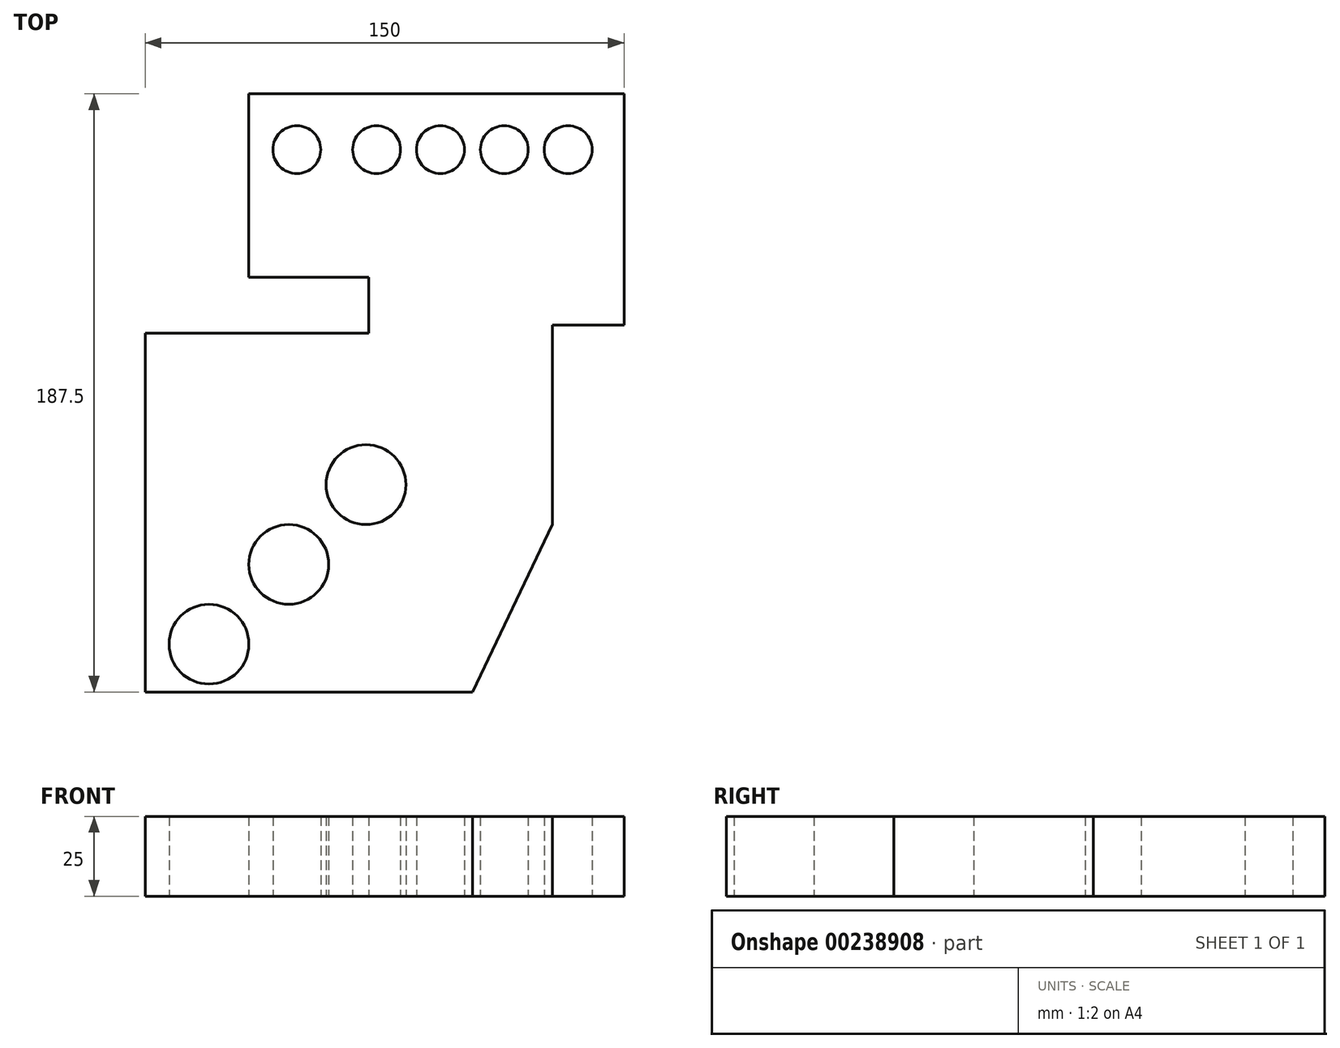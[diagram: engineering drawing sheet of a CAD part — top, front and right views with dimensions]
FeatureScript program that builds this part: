
annotation { "Feature Type Name" : "Feature", "Feature Type Description" : "" }
export const myFeature = defineFeature(function(context is Context, id is Id, definition is map)
    precondition{}
    {
        {
            var Q0;
            Q0=qCreatedBy(makeId("Top.planeOp"),FACE);
            var sketch = newSketch(context, id + "F0", { "sketchPlane" : qUnion([Q0])});
            skLineSegment(sketch, "E0", {"start": v(-72.33, -42.62) * mm, "end": v(30.17, -42.62) * mm});
            skLineSegment(sketch, "E1", {"start": v(-72.33, -42.62) * mm, "end": v(-72.33, 69.88) * mm});
            skLineSegment(sketch, "E2", {"start": v(-72.33, 69.88) * mm, "end": v(-2.33, 69.88) * mm});
            skLineSegment(sketch, "E3", {"start": v(-2.33, 69.88) * mm, "end": v(-2.33, 87.38) * mm});
            skLineSegment(sketch, "E4", {"start": v(-2.33, 87.38) * mm, "end": v(-39.83, 87.38) * mm});
            skLineSegment(sketch, "E5", {"start": v(-39.83, 87.38) * mm, "end": v(-39.83, 144.88) * mm});
            skLineSegment(sketch, "E6", {"start": v(-39.83, 144.88) * mm, "end": v(77.67, 144.88) * mm});
            skLineSegment(sketch, "E7", {"start": v(77.67, 144.88) * mm, "end": v(77.67, 72.38) * mm});
            skLineSegment(sketch, "E8", {"start": v(77.67, 72.38) * mm, "end": v(55.17, 72.38) * mm});
            skLineSegment(sketch, "E9", {"start": v(55.17, 72.38) * mm, "end": v(55.17, 9.88) * mm});
            skLineSegment(sketch, "E10", {"start": v(55.17, 9.88) * mm, "end": v(30.17, -42.62) * mm});
            skPoint(sketch, "E11.orphan", {"position": v(-52.33, -28.75) * mm});
            skCircle(sketch, "E12", {"center": v(-52.33, -27.62) * mm, "radius": 12.5 * mm});
            skPoint(sketch, "E13.end.orphan", {"position": v(-89.97, -27.62) * mm});
            skPoint(sketch, "E13.start.orphan", {"position": v(-89.97, -42.62) * mm});
            skPoint(sketch, "E14.start.orphan", {"position": v(-72.33, -56.69) * mm});
            skPoint(sketch, "E15.start.orphan", {"position": v(-29.07, -2.62) * mm});
            skCircle(sketch, "E16", {"center": v(-27.33, -2.62) * mm, "radius": 12.5 * mm});
            skPoint(sketch, "E17.start.orphan", {"position": v(-27.33, -7.55) * mm});
            skPoint(sketch, "E18.end.orphan", {"position": v(-27.33, -56.69) * mm});
            skPoint(sketch, "E19.endSnap0", {"position": v(-2.74, 25.58) * mm});
            skPoint(sketch, "E19.end.orphan", {"position": v(-2.74, -28.73) * mm});
            skPoint(sketch, "E19.start.orphan", {"position": v(-2.33, 28.79) * mm});
            skPoint(sketch, "E20.start.orphan", {"position": v(-3.15, 22.38) * mm});
            skPoint(sketch, "E21.end.orphan", {"position": v(-3.15, -11.17) * mm});
            skCircle(sketch, "E22", {"center": v(-3.15, 22.38) * mm, "radius": 12.5 * mm});
            skPoint(sketch, "E23.end.orphan", {"position": v(-2.33, -56.69) * mm});
            skCircle(sketch, "E24", {"center": v(60.17, 127.38) * mm, "radius": 7.5 * mm});
            skCircle(sketch, "E25", {"center": v(40.17, 127.38) * mm, "radius": 7.5 * mm});
            skPoint(sketch, "E26.orphan", {"position": v(15.82, 127.38) * mm});
            skCircle(sketch, "E27", {"center": v(20.17, 127.38) * mm, "radius": 7.5 * mm});
            skPoint(sketch, "E28.orphan", {"position": v(77.67, 127.38) * mm});
            skCircle(sketch, "E29", {"center": v(0.17, 127.38) * mm, "radius": 7.5 * mm});
            skCircle(sketch, "E30", {"center": v(-24.83, 127.38) * mm, "radius": 7.5 * mm});
            skPoint(sketch, "E31.end.orphan", {"position": v(87.67, 127.38) * mm});
            skSolve(sketch);
        }
        {
            var Q0;
            Q0=makeQuery(id+"F0.imprint","IMPRINT",FACE,{"disambiguationData":[TD([[makeQuery(id+"F0.imprint","IMPRINT",EDGE,{"derivedFrom":sQuery(id+"F0.wireOp",EDGE,"E0")}),1.0]])]});
            extrude(context, id + "F1", {"entities" : qUnion([Q0]), "depth" : 25 * mm});
        }
    });
